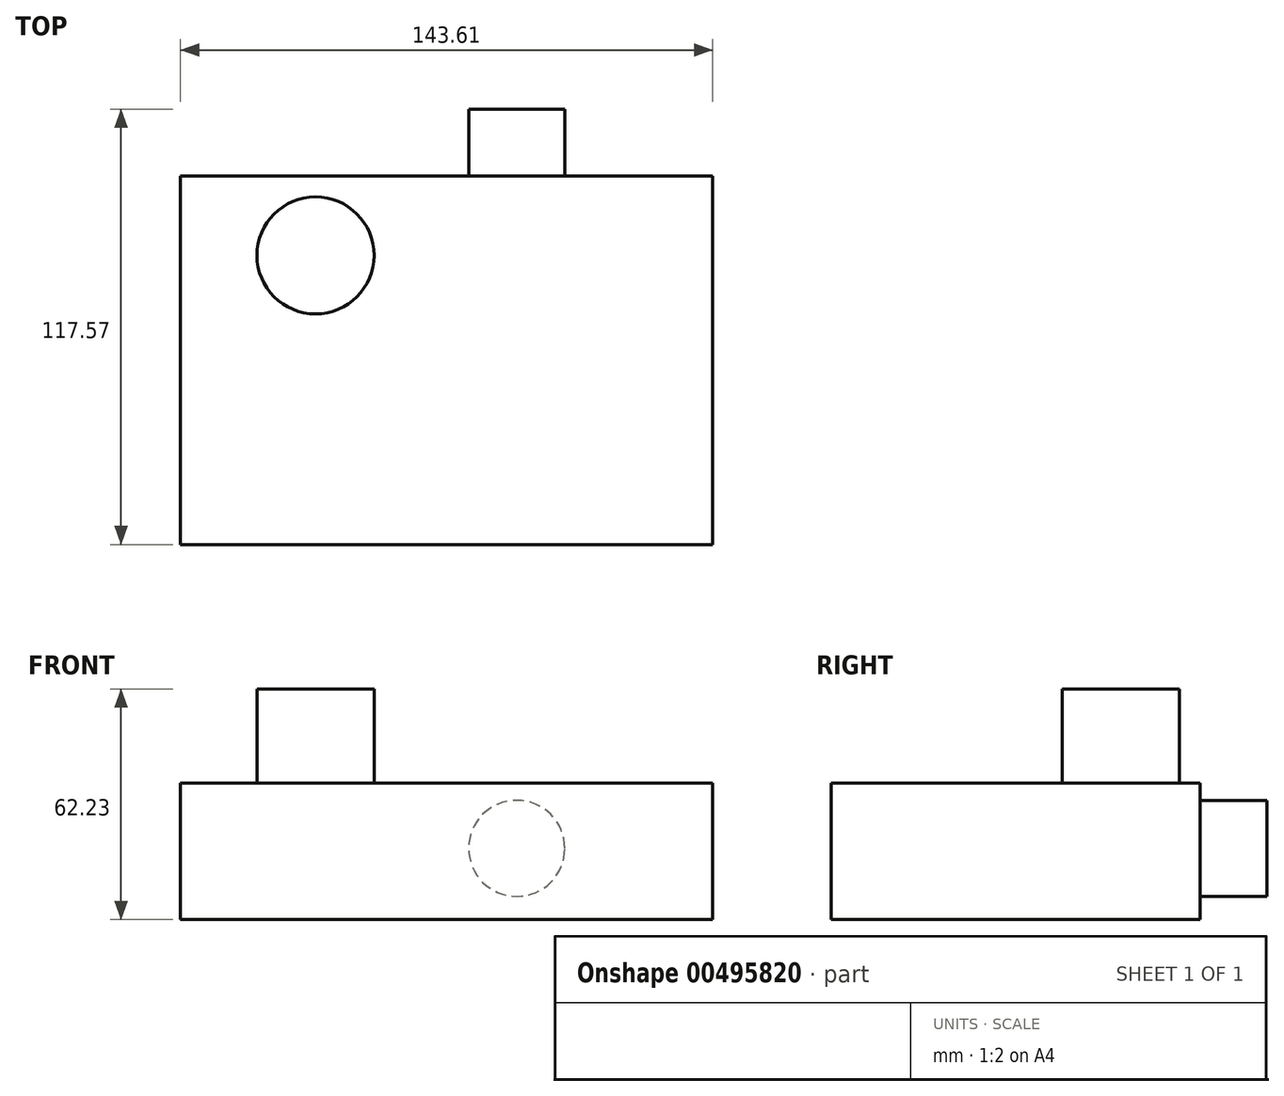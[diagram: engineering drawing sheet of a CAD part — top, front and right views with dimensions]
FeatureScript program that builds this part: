
annotation { "Feature Type Name" : "Feature", "Feature Type Description" : "" }
export const myFeature = defineFeature(function(context is Context, id is Id, definition is map)
    precondition{}
    {
        {
            var Q0;
            Q0=qCreatedBy(makeId("Top.planeOp"),FACE);
            var sketch = newSketch(context, id + "F0", { "sketchPlane" : qUnion([Q0])});
            skLineSegment(sketch, "E0.bottom", {"start": v(-126.65, 53.71) * mm, "end": v(16.96, 53.71) * mm});
            skLineSegment(sketch, "E0.top", {"start": v(-126.65, -45.82) * mm, "end": v(16.96, -45.82) * mm});
            skLineSegment(sketch, "E0.left", {"start": v(-126.65, 53.71) * mm, "end": v(-126.65, -45.82) * mm});
            skLineSegment(sketch, "E0.right", {"start": v(16.96, 53.71) * mm, "end": v(16.96, -45.82) * mm});
            skSolve(sketch);
        }
        {
            var Q0;
            Q0=makeQuery(id+"F0.imprint","IMPRINT",FACE,{"disambiguationData":[TD([[makeQuery(id+"F0.imprint","IMPRINT",EDGE,{"derivedFrom":sQuery(id+"F0.wireOp",EDGE,"E0.bottom")}),-1.0]])]});
            extrude(context, id + "F1", {"entities" : qUnion([Q0]), "depth" : 36.83 * mm});
        }
        {
            var Q0;
            Q0=makeQuery(id+"F1.opExtrude","CAP_FACE",FACE,{"disambiguationData":[OSD([sQuery(id+"F0.wireOp",EDGE,"E0.bottom"),sQuery(id+"F0.wireOp",EDGE,"E0.top"),sQuery(id+"F0.wireOp",EDGE,"E0.left"),sQuery(id+"F0.wireOp",EDGE,"E0.right")])],"isStart":false});
            var sketch = newSketch(context, id + "F2", { "sketchPlane" : qUnion([Q0])});
            skCircle(sketch, "E1", {"center": v(-90.2, 32.3) * mm, "radius": 15.8 * mm});
            skSolve(sketch);
        }
        {
            var Q0;
            Q0=makeQuery(id+"F2.imprint","IMPRINT",FACE,{"disambiguationData":[TD([[makeQuery(id+"F2.imprint","IMPRINT",EDGE,{"derivedFrom":sQuery(id+"F2.wireOp",EDGE,"E1")}),1.0]])]});
            extrude(context, id + "F3", {"entities" : qUnion([Q0]), "operationType" : NewBodyOperationType.ADD, "depth" : 25.4 * mm});
        }
        {
            var Q0;
            Q0=makeQuery(id+"F1.opExtrude","SWEPT_FACE",FACE,{"disambiguationData":[OSD([sQuery(id+"F0.wireOp",EDGE,"E0.bottom")])]});
            var sketch = newSketch(context, id + "F4", { "sketchPlane" : qUnion([Q0])});
            skCircle(sketch, "E2", {"center": v(35.9, 19.2) * mm, "radius": 12.98 * mm});
            skSolve(sketch);
        }
        {
            var Q0;
            Q0=makeQuery(id+"F4.imprint","IMPRINT",FACE,{"disambiguationData":[TD([[makeQuery(id+"F4.imprint","IMPRINT",EDGE,{"derivedFrom":sQuery(id+"F4.wireOp",EDGE,"E2")}),1.0]])]});
            extrude(context, id + "F5", {"entities" : qUnion([Q0]), "operationType" : NewBodyOperationType.ADD, "depth" : 18.03 * mm});
        }
    });
